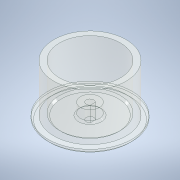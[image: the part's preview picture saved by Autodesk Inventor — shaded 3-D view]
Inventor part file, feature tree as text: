
AUTODESK INVENTOR PART (.ipt)
format: ipt  version: 2020 (Build 240168000, 168)  size: 162,304 bytes
history: native  units: mm
features: extrude x4, sketch x4, chamfer x2, plane x1
ambient origin geometry x8: Origin, YZ Plane, XZ Plane, XY Plane, X Axis, Y Axis, Z Axis, Center Point
bodies: Solid1 (feature_tree)
feature tree (11):
  extrude  "Extrusion1"  Depth=3.0mm
  extrude  "Extrusion2"  Depth=25.0mm
  plane  "Work Plane1"
  extrude  "Extrusion3"  Depth=2.0mm
  extrude  "Extrusion4"  Depth=0.5mm
  chamfer  "Chamfer1"  Distance=1.5mm
  chamfer  "Chamfer2"  Distance=28.0mm
  sketch  "Sketch1"  dims[d0=38.0mm d1=3.0mm]
  sketch  "Sketch2"  dims[d2=25.0mm d3=0.0mm d4=3.0mm]
  sketch  "Sketch3"  dims[d5=2.0mm d6=0.0mm d8=4.0mm]
  sketch  "Sketch4"  dims[d9=9.0mm d10=4.5mm d11=1.5mm d12=28.0mm d13=0.0mm d14=3.0mm d15=4.0mm d16=6.0mm d17=0.0mm d21=1.0mm d22=2.0mm d23=45.0deg d24=1.0mm d25=2.0mm d26=45.0deg d18=0.5mm d19=0.872665mm d20=0.5mm]
